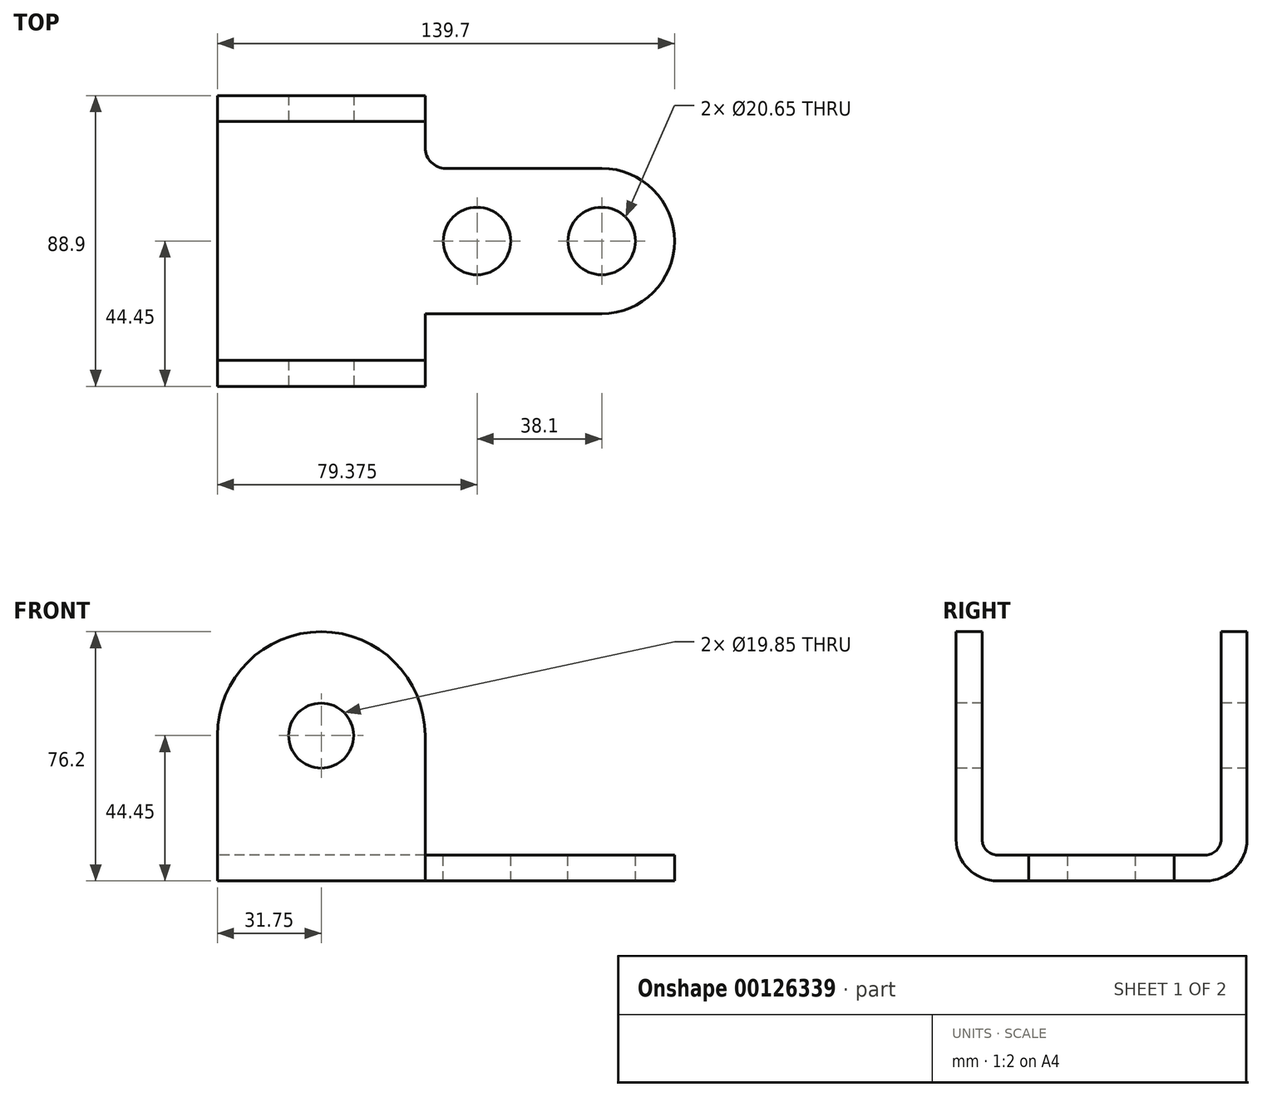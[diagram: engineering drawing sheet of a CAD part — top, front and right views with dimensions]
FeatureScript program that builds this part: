
annotation { "Feature Type Name" : "Feature", "Feature Type Description" : "" }
export const myFeature = defineFeature(function(context is Context, id is Id, definition is map)
    precondition{}
    {
        {
            var Q0;
            Q0=qCreatedBy(makeId("Right.planeOp"),FACE);
            var sketch = newSketch(context, id + "F0", { "sketchPlane" : qUnion([Q0])});
            skLineSegment(sketch, "E0", {"start": v(0, 0) * mm, "end": v(0, 85.68) * mm, "construction": true});
            skLineSegment(sketch, "E1", {"start": v(-44.45, 44.45) * mm, "end": v(-44.45, 12.7) * mm});
            skLineSegment(sketch, "E2", {"start": v(-31.75, 0) * mm, "end": v(0, 0) * mm});
            skLineSegment(sketch, "E3", {"start": v(-44.45, 44.45) * mm, "end": v(-36.51, 44.45) * mm});
            skLineSegment(sketch, "E4", {"start": v(-36.51, 44.45) * mm, "end": v(-36.51, 12.7) * mm});
            skLineSegment(sketch, "E5", {"start": v(-31.75, 7.94) * mm, "end": v(0, 7.94) * mm});
            skPoint(sketch, "E6.visualSharp", {"position": v(-44.45, 0) * mm});
            skArc(sketch, "E6.filletArc", {"start": v(-44.45, 12.7) * mm, "mid": v(-40.73, 3.72) * mm, "end": v(-31.75, 0) * mm});
            skPoint(sketch, "E7.visualSharp", {"position": v(-36.51, 7.94) * mm});
            skArc(sketch, "E7.filletArc", {"start": v(-36.51, 12.7) * mm, "mid": v(-35.12, 9.33) * mm, "end": v(-31.75, 7.94) * mm});
            skArc(sketch, "E8.MirrorCS", {"start": v(36.51, 12.7) * mm, "mid": v(35.12, 9.33) * mm, "end": v(31.75, 7.94) * mm});
            skArc(sketch, "E9.MirrorCS", {"start": v(44.45, 12.7) * mm, "mid": v(40.73, 3.72) * mm, "end": v(31.75, 0) * mm});
            skLineSegment(sketch, "E10.MirrorCS", {"start": v(44.45, 44.45) * mm, "end": v(44.45, 12.7) * mm});
            skLineSegment(sketch, "E11.MirrorCS", {"start": v(31.75, 7.94) * mm, "end": v(0, 7.94) * mm});
            skPoint(sketch, "E12.MirrorP", {"position": v(36.51, 7.94) * mm});
            skLineSegment(sketch, "E13.MirrorCS", {"start": v(36.51, 44.45) * mm, "end": v(36.51, 12.7) * mm});
            skLineSegment(sketch, "E14.MirrorCS", {"start": v(0, 7.94) * mm, "end": v(0, 0) * mm});
            skLineSegment(sketch, "E15.MirrorCS", {"start": v(44.45, 44.45) * mm, "end": v(36.51, 44.45) * mm});
            skPoint(sketch, "E16.MirrorP", {"position": v(44.45, 0) * mm});
            skLineSegment(sketch, "E17.MirrorCS", {"start": v(31.75, 0) * mm, "end": v(0, 0) * mm});
            skSolve(sketch);
        }
        {
            var Q0;
            Q0=qSketchRegion(id+"F0",true);
            extrude(context, id + "F1", {"entities" : qUnion([Q0]), "depth" : 63.5 * mm});
        }
        {
            var Q0;
            Q0=makeQuery(id+"F1.opExtrude","SWEPT_FACE",FACE,{"disambiguationData":[OSD([sQuery(id+"F0.wireOp",EDGE,"E1")])]});
            var sketch = newSketch(context, id + "F2", { "sketchPlane" : qUnion([Q0])});
            skArc(sketch, "E18", {"start": v(63.5, 44.45) * mm, "mid": v(31.75, 76.2) * mm, "end": v(0, 44.45) * mm});
            skLineSegment(sketch, "E19", {"start": v(0, 44.45) * mm, "end": v(63.5, 44.45) * mm});
            skSolve(sketch);
        }
        {
            var Q0;
            Q0=qSketchRegion(id+"F2",true);
            var Q1;
            Q1=makeQuery(id+"F1.opExtrude","SWEPT_FACE",FACE,{"disambiguationData":[OSD([sQuery(id+"F0.wireOp",EDGE,"E4")])]});
            extrude(context, id + "F3", {"entities" : qUnion([Q0]), "operationType" : NewBodyOperationType.ADD, "endBound" : BoundingType.UP_TO_SURFACE, "oppositeDirection" : true, "endBoundEntityFace" : qUnion([Q1]), "depth" : 25.4 * mm});
        }
        {
            var Q0;
            Q0=makeQuery(id+"F1.opExtrude","SWEPT_FACE",FACE,{"disambiguationData":[OSD([sQuery(id+"F0.wireOp",EDGE,"E10.MirrorCS")])]});
            var sketch = newSketch(context, id + "F4", { "sketchPlane" : qUnion([Q0])});
            skArc(sketch, "E20.0", {"start": v(-63.5, 44.45) * mm, "mid": v(-31.75, 76.2) * mm, "end": v(0, 44.45) * mm});
            skLineSegment(sketch, "E21.0", {"start": v(0, 44.45) * mm, "end": v(-63.5, 44.45) * mm});
            skSolve(sketch);
        }
        {
            var Q0;
            Q0=qSketchRegion(id+"F4",true);
            var Q1;
            Q1=makeQuery(id+"F1.opExtrude","SWEPT_FACE",FACE,{"disambiguationData":[OSD([sQuery(id+"F0.wireOp",EDGE,"E13.MirrorCS")])]});
            extrude(context, id + "F5", {"entities" : qUnion([Q0]), "operationType" : NewBodyOperationType.ADD, "endBound" : BoundingType.UP_TO_SURFACE, "oppositeDirection" : true, "endBoundEntityFace" : qUnion([Q1]), "depth" : 25.4 * mm});
        }
        {
            var Q0;
            Q0=makeQuery(id+"F1.opExtrude","SWEPT_FACE",FACE,{"disambiguationData":[OSD([sQuery(id+"F0.wireOp",EDGE,"E2"),sQuery(id+"F0.wireOp",EDGE,"E17.MirrorCS")])]});
            var sketch = newSketch(context, id + "F6", { "sketchPlane" : qUnion([Q0])});
            skLineSegment(sketch, "E22", {"start": v(0, 0) * mm, "end": v(171.63, 0) * mm, "construction": true});
            skPoint(sketch, "E22.endSnap0", {"position": v(63.5, 0) * mm});
            skLineSegment(sketch, "E23", {"start": v(63.5, -22.23) * mm, "end": v(117.47, -22.23) * mm});
            skArc(sketch, "E24", {"start": v(117.47, -22.23) * mm, "mid": v(133.2, -15.72) * mm, "end": v(139.7, 0) * mm});
            skLineSegment(sketch, "E25.MirrorCS", {"start": v(63.5, 22.23) * mm, "end": v(117.47, 22.23) * mm});
            skArc(sketch, "E26.MirrorCS", {"start": v(117.47, 22.23) * mm, "mid": v(133.2, 15.72) * mm, "end": v(139.7, 0) * mm});
            skLineSegment(sketch, "E27", {"start": v(63.5, -22.23) * mm, "end": v(63.5, 22.23) * mm});
            skSolve(sketch);
        }
        {
            var Q0;
            Q0=qSketchRegion(id+"F6",true);
            var Q1;
            Q1=makeQuery(id+"F1.opExtrude","SWEPT_FACE",FACE,{"disambiguationData":[OSD([sQuery(id+"F0.wireOp",EDGE,"E5"),sQuery(id+"F0.wireOp",EDGE,"E11.MirrorCS")])]});
            extrude(context, id + "F7", {"entities" : qUnion([Q0]), "operationType" : NewBodyOperationType.ADD, "endBound" : BoundingType.UP_TO_SURFACE, "oppositeDirection" : true, "endBoundEntityFace" : qUnion([Q1]), "depth" : 25.4 * mm});
        }
        {
            var Q0;
            Q0=makeQuery(id+"F7.opExtrude","SWEPT_EDGE",EDGE,{"disambiguationData":[OSD([sQuery(id+"F0.wireOp",EDGE,"E2"),sQuery(id+"F0.wireOp",EDGE,"E17.MirrorCS"),sQuery(id+"F6.wireOp",EDGE,"E25.MirrorCS"),sQuery(id+"F6.wireOp",EDGE,"E27")])]});
            var Q1;
            Q1=makeQuery(id+"F7.opExtrude","SWEPT_EDGE",EDGE,{"disambiguationData":[OSD([sQuery(id+"F0.wireOp",EDGE,"E2"),sQuery(id+"F0.wireOp",EDGE,"E17.MirrorCS"),sQuery(id+"F6.wireOp",EDGE,"E23"),sQuery(id+"F6.wireOp",EDGE,"E27")])]});
            fillet(context, id + "F8", {"entities" : qUnion([Q0, Q1]), "radius" : 6.35 * mm, "tangentPropagation" : true, "allowEdgeOverflow" : false});
        }
        {
            var Q0;
            Q0=makeQuery(id+"F2.imprint","IMPRINT",FACE,{"disambiguationData":[TD([[makeQuery(id+"F2.imprint","IMPRINT",EDGE,{"derivedFrom":sQuery(id+"F2.wireOp",EDGE,"E18")}),1.0]])]});
            var sketch = newSketch(context, id + "F9", { "sketchPlane" : qUnion([Q0])});
            skCircle(sketch, "E28", {"center": v(31.75, 44.45) * mm, "radius": 9.92 * mm});
            skSolve(sketch);
        }
        {
            var Q0;
            Q0=qSketchRegion(id+"F9",true);
            extrude(context, id + "F10", {"entities" : qUnion([Q0]), "operationType" : NewBodyOperationType.REMOVE, "endBound" : BoundingType.THROUGH_ALL, "oppositeDirection" : true, "depth" : 25.4 * mm});
        }
        {
            var Q0;
            {var subQ0=sQuery(id+"F0.wireOp",EDGE,"E11.MirrorCS");var subQ1=sQuery(id+"F0.wireOp",EDGE,"E5");Q0=makeQuery(id+"F7.boolean.opBoolean","MERGE",FACE,{"derivedFrom":[makeQuery(id+"F1.opExtrude","SWEPT_FACE",FACE,{"disambiguationData":[OSD([subQ1,subQ0])]}),makeQuery(id+"F7.opExtrude","CAP_FACE",FACE,{"disambiguationData":[OSD([subQ1,subQ0])],"isStart":false})]});}
            var sketch = newSketch(context, id + "F11", { "sketchPlane" : qUnion([Q0])});
            skCircle(sketch, "E29", {"center": v(117.47, 0) * mm, "radius": 10.33 * mm});
            skCircle(sketch, "E30", {"center": v(79.38, 0) * mm, "radius": 10.33 * mm});
            skSolve(sketch);
        }
        {
            var Q0;
            Q0=qSketchRegion(id+"F11",true);
            extrude(context, id + "F12", {"entities" : qUnion([Q0]), "operationType" : NewBodyOperationType.REMOVE, "endBound" : BoundingType.THROUGH_ALL, "oppositeDirection" : true, "depth" : 25.4 * mm});
        }
    });
